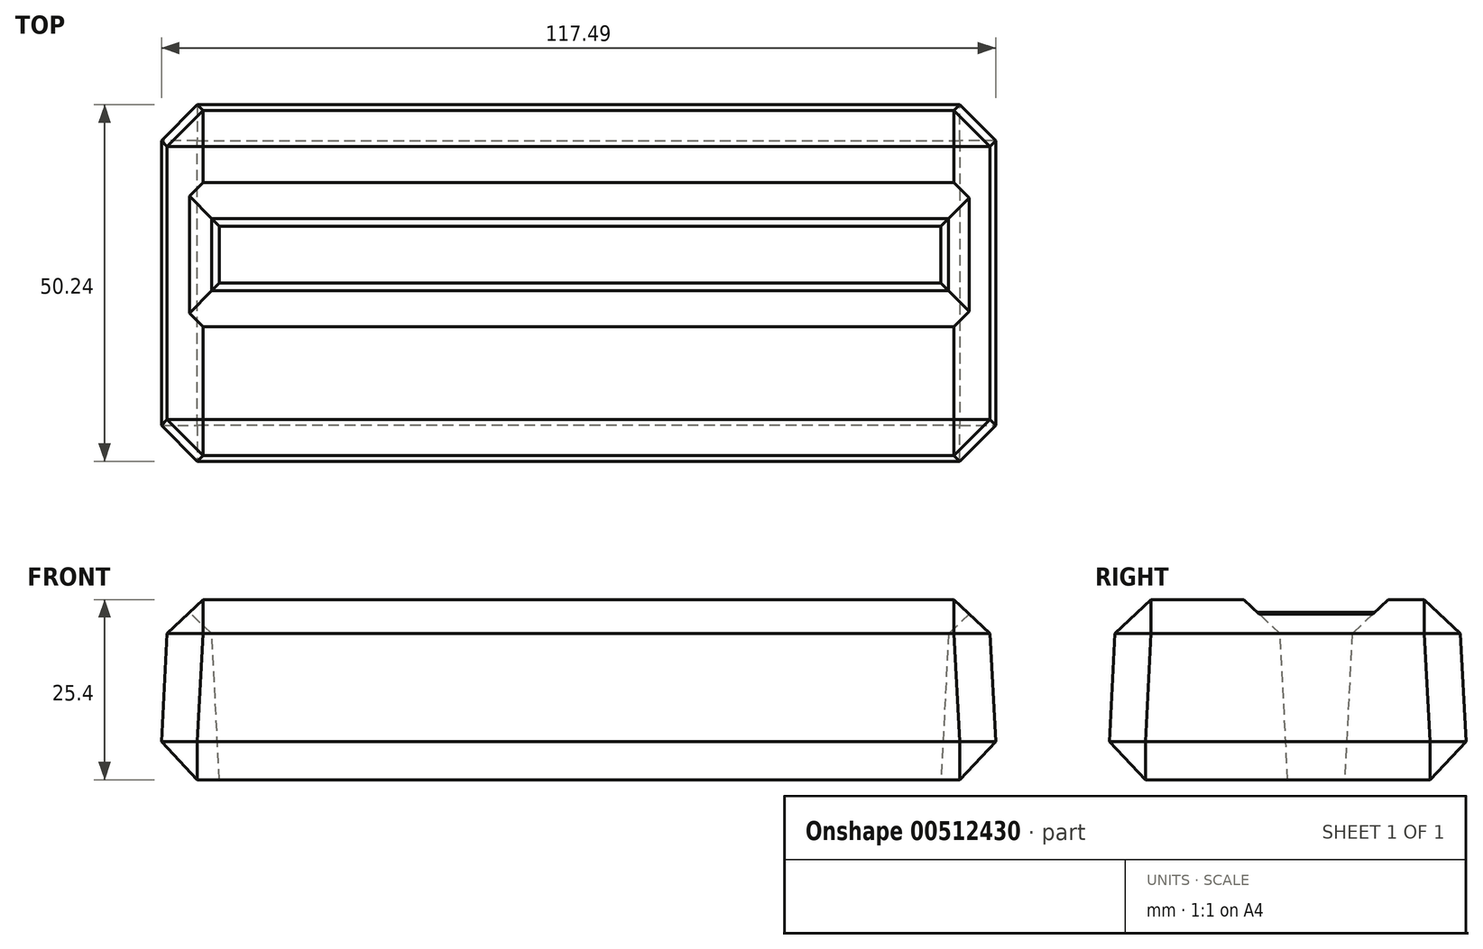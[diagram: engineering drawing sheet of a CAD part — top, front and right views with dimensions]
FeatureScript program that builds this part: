
annotation { "Feature Type Name" : "Feature", "Feature Type Description" : "" }
export const myFeature = defineFeature(function(context is Context, id is Id, definition is map)
    precondition{}
    {
        {
            var Q0;
            Q0=qCreatedBy(makeId("Top.planeOp"),FACE);
            var sketch = newSketch(context, id + "F0", { "sketchPlane" : qUnion([Q0])});
            skLineSegment(sketch, "E0", {"start": v(-45.2, -8) * mm, "end": v(56.4, -8) * mm});
            skLineSegment(sketch, "E1.top", {"start": v(-45.2, 0) * mm, "end": v(56.4, 0) * mm});
            skLineSegment(sketch, "E1.left", {"start": v(-45.2, -8) * mm, "end": v(-45.2, 0) * mm});
            skLineSegment(sketch, "E1.right", {"start": v(56.4, -8) * mm, "end": v(56.4, 0) * mm});
            skLineSegment(sketch, "E2.right", {"start": v(-53.66, 17.4) * mm, "end": v(-53.66, -33.4) * mm});
            skLineSegment(sketch, "E3.right", {"start": v(64.4, -33.4) * mm, "end": v(64.4, 17.4) * mm});
            skLineSegment(sketch, "E4", {"start": v(-53.66, -33.4) * mm, "end": v(64.4, -33.4) * mm});
            skLineSegment(sketch, "E5", {"start": v(-53.66, 17.4) * mm, "end": v(64.4, 17.4) * mm});
            skSolve(sketch);
        }
        {
            var Q0;
            Q0=makeQuery(id+"F0.imprint","IMPRINT",FACE,{"disambiguationData":[TD([[makeQuery(id+"F0.imprint","IMPRINT",EDGE,{"derivedFrom":sQuery(id+"F0.wireOp",EDGE,"E0")}),-1.0]])]});
            extrude(context, id + "F1", {"entities" : qUnion([Q0]), "depth" : 25.4 * mm, "hasDraft" : true, "draftAngle" : 3 * degree, "draftPullDirection" : true});
        }
        {
            var Q0;
            Q0=makeQuery(id+"F1.opExtrude","SWEPT_FACE",FACE,{"disambiguationData":[OSD([sQuery(id+"F0.wireOp",EDGE,"E4")])]});
            var Q1;
            Q1=makeQuery(id+"F1.opExtrude","CAP_FACE",FACE,{"disambiguationData":[OSD([sQuery(id+"F0.wireOp",EDGE,"E0"),sQuery(id+"F0.wireOp",EDGE,"E1.top"),sQuery(id+"F0.wireOp",EDGE,"E1.left"),sQuery(id+"F0.wireOp",EDGE,"E1.right"),sQuery(id+"F0.wireOp",EDGE,"E2.right"),sQuery(id+"F0.wireOp",EDGE,"E3.right"),sQuery(id+"F0.wireOp",EDGE,"E4"),sQuery(id+"F0.wireOp",EDGE,"E5")])],"isStart":false});
            var Q2;
            Q2=makeQuery(id+"F1.opExtrude","SWEPT_FACE",FACE,{"disambiguationData":[OSD([sQuery(id+"F0.wireOp",EDGE,"E3.right")])]});
            var Q3;
            Q3=makeQuery(id+"F1.opExtrude","SWEPT_FACE",FACE,{"disambiguationData":[OSD([sQuery(id+"F0.wireOp",EDGE,"E5")])]});
            var Q4;
            Q4=makeQuery(id+"F1.opExtrude","SWEPT_FACE",FACE,{"disambiguationData":[OSD([sQuery(id+"F0.wireOp",EDGE,"E2.right")])]});
            chamfer(context, id + "F2", {"entities" : qUnion([Q0, Q1, Q2, Q3, Q4]), "width" : 5.08 * mm, "tangentPropagation" : true});
        }
    });
